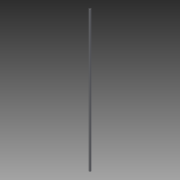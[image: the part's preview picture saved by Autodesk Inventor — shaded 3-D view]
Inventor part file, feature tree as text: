
AUTODESK INVENTOR PART (.ipt)
format: ipt  version: 2015 SP1 (Build 190203100, 203)  size: 75,264 bytes
history: native  units: mm
features: extrude x1, sketch x1
ambient origin geometry x8: Origin, YZ Plane, XZ Plane, XY Plane, X Axis, Y Axis, Z Axis, Center Point
bodies: Solid1 (feature_tree)
feature tree (2):
  extrude  "Extrusion1"  Depth=20.0mm
  sketch  "Sketch1"  dims[d0=20.0mm d1=20.0mm d2=2.0mm d3=2200.0mm d4=0.0mm]
